# Revit family: Смесительный клапан системы водоснабжения 7766 54
name_source: partatom
category: Rohrzubehör
units: mm (PartAtom-declared; Revit-internal decimal feet)

## family parameters
Arbeitsebenenbasiert = Nein
Beim Laden mit Abzugskörper schneiden = Nein
Bemaßung runder Anschluss = Durchmesser verwenden
Gemeinsam genutzt = Nein
Immer vertikal = Ja
OmniClass-Nummer = 23.65.55.14
OmniClass-Titel = Valves for Liquid Services
Teiletyp = Unterbricht

## types (1)
- Смесительный клапан системы водоснабжения 7766 54
    H00 = 82 mm
    H01 = 21 mm  [stored 0.0688976 ft]
    H02 = 9 mm  [stored 0.0295276 ft]
    H03 = 14 mm  [stored 0.0459318 ft]
    H04 = 35 mm
    H05 = 3 mm  [stored 0.00984252 ft]
    H06 = 25 mm  [stored 0.082021 ft]
    H07 = 62 mm
    H08 = 8 mm  [stored 0.0262467 ft]
    Hersteller = HERZ Armaturen Ges.m.b.H.
    L00 = 40 mm  [stored 0.131234 ft]
    L01 = 12 mm  [stored 0.0393701 ft]
    L02 = 21 mm  [stored 0.0688976 ft]
    LO1 = 59 mm
    Nennweite = 20 mm  [stored 0.0656168 ft]
    R01 = 8 mm  [stored 0.0262467 ft]
    R02 = 10 mm  [stored 0.0328084 ft]
    R03 = 12 mm  [stored 0.0393701 ft]
    R04 = 24 mm
    R05 = 20 mm  [stored 0.0656168 ft]
    R06 = 24 mm
    R07 = 4 mm  [stored 0.0131234 ft]
    S01 = 61 mm
    S02 = 38 mm
    SCTWCODE = 04;18;03
    SCTWSEQ = AW;SBT_TYP_AW="104";3
    URL = www.herz-armaturen.ru
    Vorgabe-Ansicht = 0 mm  [stored 0 ft]
    Внутренние части = латунь, устойчивая к селективной цинковой коррозии, CW626N
    Диапазон установки = 35 °C - 50 °C
    Корпус = латунь, устойчивая к селективной цинковой коррозии, CC770S
    Макс. рабочая температура (горячая вода) = 85 °C
    Макс. рабочее давление (динамическое) = 0.2 - 6 bar
    Маховик = ABS
    Мин. превышение температуры горячей воды над температурой воды в смесителе = 15 °C
    Мин. рабочая температура (холодная вода) = 5 °C - 25 °C
    Мин. расход = 0.1 L/s
    Номер заказа = 2776654
    Примечание = В соответствии со статьей 33 Регламента REACH (Registration; Evaluation; Authorisation; Restriction of Chemicals) (EC № 1907/2006) мы обязаны указать, что свинец внесен в список SVHC (Substances of Very High Concern - вещества очень высокой важности) и весовой процент свинца во всех латунных компонентах заводского изготовления в наших изделиях, превышает 0,1 % (w/w) (CAS: 7439-92-1 / EINECS: 231-100-4).
Поскольку свинец является легирующим компонентом сплава, прямое негативное влияние исключается, и поэтому дополнительной информации о безопасном использовании не требуется.
    Принцип работы = Термостатический смесительный клапан 7766 TMV применяется в системах с теплой питьевой водой.
Независимо от изменений давления или температуры холодной и горячей воды, смешиваемой в клапане, смешанная вода постоянно регулируется до заданной температуры и расхода.
Термостатический клапан работает независимо и без дополнительной энергии.
После монтажа предварительно настроенное значение желаемой температуры смешивания поддерживается постоянным в пределах гистерезиса регулирования.
    Пружина = нержавеющая сталь 1.4310
    Рабочее давление (статическое) = 1000000.0 Pa
    Расход при давлении 3 бар = 0.7 L/s
    Резьба для подключения = плоское уплотнение, G 3/4
    Среда = Питьевая вода
    Температура смешения (заводская настройка) = 45 °C
    Температурная стабильность на выходе = +-2°C
    Указания по безопасности = Cмесительный клапан для систем питьевого водоснабжения выполняет функцию защитaы от ожога.
Его рекомендуется заменять каждые 5 лет.
Местные стандарты и правила должны соблюдаться.
    Указания по техническому обслуживанию = • Рекомендуется проведение проверки не реже одного раза в год.
   При использовании воды плохого или неизвестного качества проверки следует проводить чаще.
• Проверки температуры воды на выходе должны выполняться точно таким же способом, как и при первичной установке; значение этой температуры не должно отличаться от заданной температуры более, чем на + / - 2 °С.
• Обратные клапаны легко доступны для чистки.
   Рекомендуется использовать плоскогубцы с удлиненными губками для того, чтобы избежать повреждений обратного клапана при его извлечении.
• Помимо снятия маховика и очистки обратного клапана дальнейший демонтаж клапана для технического обслуживания не требуется.
    Уплотнение = EPDM
    Шпиндель = латунь, устойчивая к селективной цинковой коррозии, CW626N

note: [stored X ft] marks values corroborated as IEEE doubles in the binary element streams (Revit-internal decimal feet)
